# Revit family: Ulimax_Madeira_Porta-de-Giro-1-Folha
name_source: partatom
category: Doors
units: mm (PartAtom-declared; Revit-internal decimal feet)

## family parameters
Always vertical = Yes
Cut with Voids When Loaded = No
Host = Wall
OmniClass Number = 23.30.10.00
OmniClass Title = Doors
Room Calculation Point = No
Shared = No

## types (12) — shared parameters
4.5cm = Yes
5.5cm = No
6.5cm = No
Altura Maçaneta = 110 cm
Analytic Construction = <Nenhum>
Define Thermal Properties by = Schematic Type
Description = Porta com esquadria de madeira, 1 Folha
Developer = Blocks
Espessura     ‎ = 1.3 cm
Guarnição Interna = Yes
Guarnição‎ Externa = Yes
Height = 210 cm
Largura‎ ‎ = 7 cm
Manufacturer = Ulimax&Co
Maçaneta = Yes
Maçaneta ‎ ‎ = Ulimax - Metal - Chrome - 203-203-203
Rough Height = 220 cm
Thickness = 4.5 cm
Type Comments = Porta de Giro de Madeira
URL = https://www.ulimax.com.br
URL Developer = https://BlocksRvt.com
URL Produto = https://www.ulimax.com.br
URL Template = https://www.ulimax.com.br
Wall Closure = By host

## per-type parameters (varying)
| type | Batente | Folha | Guarnição | Rough Width | Width |
| Cedro Arana - 0.70 x 2.10 | Ulimax - Wood - Cedro Arana | Ulimax - Wood - Cedro Arana | Ulimax - Wood - Cedro Arana | 80 cm | 70 cm |
| Cedro Arana - 0.80 x 2.10 | Ulimax - Wood - Cedro Arana | Ulimax - Wood - Cedro Arana | Ulimax - Wood - Cedro Arana | 90 cm | 80 cm |
| Cedro Arana - 0.90 x 2.10 | Ulimax - Wood - Cedro Arana | Ulimax - Wood - Cedro Arana | Ulimax - Wood - Cedro Arana | 100 cm | 90 cm |
| Cedro Arana - 0.60 x 2.10 | Ulimax - Wood - Cedro Arana | Ulimax - Wood - Cedro Arana | Ulimax - Wood - Cedro Arana | 70 cm | 60 cm |
| Cumarú - 0.70 x 2.10 | Ulimax - Wood - Cumarú | Ulimax - Wood - Cumarú | Ulimax - Wood - Cumarú | 80 cm | 70 cm |
| Cumarú - 0.60 x 2.10 | Ulimax - Wood - Cumarú | Ulimax - Wood - Cumarú | Ulimax - Wood - Cumarú | 70 cm | 60 cm |
| Cumarú - 0.80 x 2.10 | Ulimax - Wood - Cumarú | Ulimax - Wood - Cumarú | Ulimax - Wood - Cumarú | 90 cm | 80 cm |
| Cumarú - 0.90 x 2.10 | Ulimax - Wood - Cumarú | Ulimax - Wood - Cumarú | Ulimax - Wood - Cumarú | 100 cm | 90 cm |
| Freijó - 0.70 x 2.10 | Ulimax - Wood - Freijo | Ulimax - Wood - Freijo | Ulimax - Wood - Freijo | 80 cm | 70 cm |
| Freijó - 0.80 x 2.10 | Ulimax - Wood - Freijo | Ulimax - Wood - Freijo | Ulimax - Wood - Freijo | 90 cm | 80 cm |
| Freijó - 0.90 x 2.10 | Ulimax - Wood - Freijo | Ulimax - Wood - Freijo | Ulimax - Wood - Freijo | 100 cm | 90 cm |
| Freijó - 0.60 x 2.10 | Ulimax - Wood - Freijo | Ulimax - Wood - Freijo | Ulimax - Wood - Freijo | 70 cm | 60 cm |
